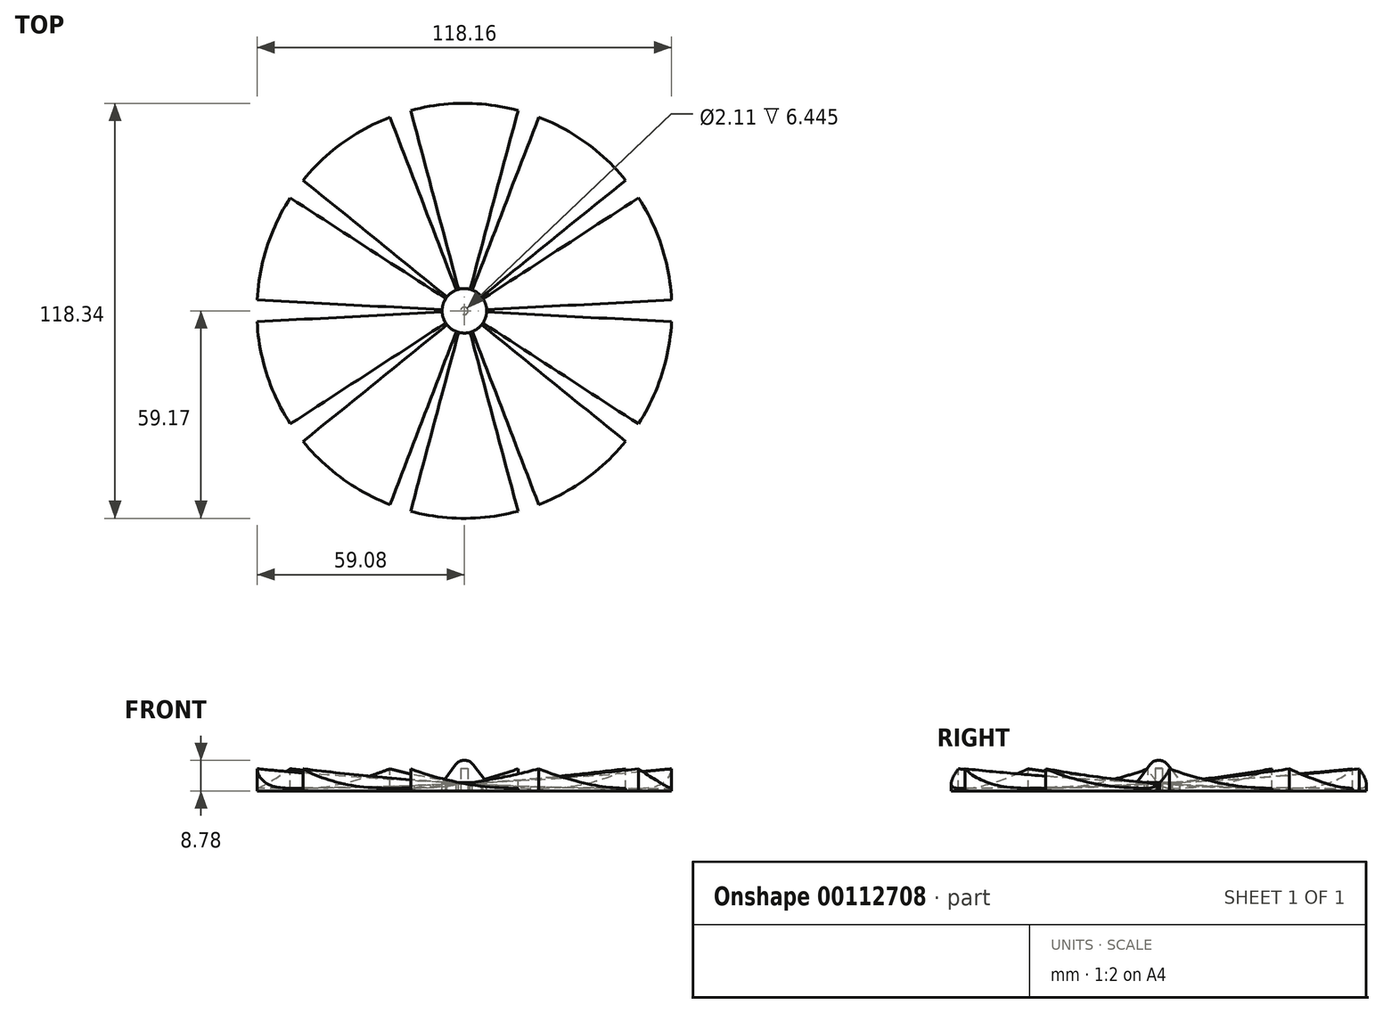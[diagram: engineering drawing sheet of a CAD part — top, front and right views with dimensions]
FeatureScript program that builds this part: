
annotation { "Feature Type Name" : "Feature", "Feature Type Description" : "" }
export const myFeature = defineFeature(function(context is Context, id is Id, definition is map)
    precondition{}
    {
        {
            var Q0;
            Q0=qCreatedBy(makeId("Top.planeOp"),FACE);
            var sketch = newSketch(context, id + "F0", { "sketchPlane" : qUnion([Q0])});
            skLineSegment(sketch, "E0", {"start": v(-15.31, -57.15) * mm, "end": v(15.31, -57.15) * mm, "construction": true});
            skLineSegment(sketch, "E1", {"start": v(0, 0) * mm, "end": v(0, -57.15) * mm, "construction": true});
            skArc(sketch, "E2", {"start": v(-15.31, -57.15) * mm, "mid": v(0, -59.17) * mm, "end": v(15.31, -57.15) * mm});
            skLineSegment(sketch, "E3", {"start": v(15.31, -57.15) * mm, "end": v(1.7, -6.35) * mm});
            skLineSegment(sketch, "E4", {"start": v(-15.31, -57.15) * mm, "end": v(-1.7, -6.35) * mm});
            skLineSegment(sketch, "E5", {"start": v(0, 0) * mm, "end": v(-1.7, -6.35) * mm});
            skLineSegment(sketch, "E6", {"start": v(0, 0) * mm, "end": v(1.7, -6.35) * mm});
            skLineSegment(sketch, "E7", {"start": v(1.7, -6.35) * mm, "end": v(-1.7, -6.35) * mm, "construction": true});
            skCircle(sketch, "E8", {"center": v(0, 0) * mm, "radius": 6.35 * mm, "construction": true});
            skSolve(sketch);
        }
        {
            var Q0;
            Q0 = qSketchRegion(id + "F0", true);
            extrude(context, id + "F1", {"entities" : qUnion([Q0]), "depth" : 6.35 * mm});
        }
        {
            var Q0;
            Q0=qCreatedBy(makeId("Front.planeOp"),FACE);
            var sketch = newSketch(context, id + "F2", { "sketchPlane" : qUnion([Q0])});
            skLineSegment(sketch, "E9.bottom", {"start": v(15.31, 0) * mm, "end": v(-15.31, 0) * mm, "construction": true});
            skLineSegment(sketch, "E9.top", {"start": v(15.31, 6.35) * mm, "end": v(-15.31, 6.35) * mm});
            skLineSegment(sketch, "E9.left", {"start": v(-15.31, 0) * mm, "end": v(-15.31, 6.35) * mm, "construction": true});
            skLineSegment(sketch, "E9.right", {"start": v(15.31, 0.8) * mm, "end": v(15.31, 6.35) * mm});
            skLineSegment(sketch, "E10", {"start": v(15.31, 0) * mm, "end": v(15.31, 0.8) * mm});
            skLineSegment(sketch, "E11", {"start": v(-15.31, 0.8) * mm, "end": v(15.31, 0.8) * mm, "construction": true});
            skArc(sketch, "E12", {"start": v(-15.31, 6.35) * mm, "mid": v(-0.25, 2.2) * mm, "end": v(15.31, 0.8) * mm});
            skSolve(sketch);
        }
        {
            var Q0;
            Q0 = qSketchRegion(id + "F2", true);
            var Q1;
            Q1=makeQuery(id+"F1.opExtrude","SWEPT_FACE",FACE,{"disambiguationData":[OSD([sQuery(id+"F0.wireOp",EDGE,"E2")])]});
            extrude(context, id + "F3", {"entities" : qUnion([Q0]), "operationType" : NewBodyOperationType.REMOVE, "endBound" : BoundingType.UP_TO_SURFACE, "endBoundEntityFace" : qUnion([Q1]), "depth" : 25.4 * mm});
        }
        {
            var Q0;
            Q0=makeQuery(id+"F1.opExtrude","CAP_FACE",FACE,{"disambiguationData":[OSD([sQuery(id+"F0.wireOp",EDGE,"E2"),sQuery(id+"F0.wireOp",EDGE,"E3"),sQuery(id+"F0.wireOp",EDGE,"E4"),sQuery(id+"F0.wireOp",EDGE,"E5"),sQuery(id+"F0.wireOp",EDGE,"E6")])],"isStart":true});
            var sketch = newSketch(context, id + "F4", { "sketchPlane" : qUnion([Q0])});
            skLineSegment(sketch, "E13", {"start": v(-15.31, 57.15) * mm, "end": v(-15.31, 57.15) * mm});
            skLineSegment(sketch, "E14", {"start": v(-15.31, 57.15) * mm, "end": v(0, 0) * mm});
            skLineSegment(sketch, "E15", {"start": v(0, 0) * mm, "end": v(15.31, 57.15) * mm});
            skLineSegment(sketch, "E16", {"start": v(15.31, 57.15) * mm, "end": v(15.31, 57.15) * mm});
            skArc(sketch, "E17", {"start": v(15.31, 57.15) * mm, "mid": v(0, 59.17) * mm, "end": v(-15.31, 57.15) * mm, "construction": true});
            skArc(sketch, "E18", {"start": v(-15.31, 57.15) * mm, "mid": v(0, -59.17) * mm, "end": v(15.31, 57.15) * mm});
            skSolve(sketch);
        }
        {
            var Q0;
            Q0 = qSketchRegion(id + "F4", true);
            extrude(context, id + "F5", {"entities" : qUnion([Q0]), "operationType" : NewBodyOperationType.ADD, "oppositeDirection" : true, "depth" : 6.35 * mm});
        }
        {
            var Q0;
            Q0=makeQuery(id+"F5.opExtrude","CAP_FACE",FACE,{"disambiguationData":[OSD([sQuery(id+"F4.wireOp",EDGE,"E13"),sQuery(id+"F4.wireOp",EDGE,"E14"),sQuery(id+"F4.wireOp",EDGE,"E15"),sQuery(id+"F4.wireOp",EDGE,"E16"),sQuery(id+"F4.wireOp",EDGE,"E18")])],"isStart":false});
            var sketch = newSketch(context, id + "F6", { "sketchPlane" : qUnion([Q0])});
            skCircle(sketch, "E19", {"center": v(0, 0) * mm, "radius": 6.35 * mm});
            skSolve(sketch);
        }
        {
            var Q0;
            Q0 = qSketchRegion(id + "F6", true);
            var Q1;
            Q1=makeQuery(id+"F5.boolean.opBoolean","MERGE",FACE,{"derivedFrom":[makeQuery(id+"F1.opExtrude","CAP_FACE",FACE,{"disambiguationData":[OSD([sQuery(id+"F0.wireOp",EDGE,"E2"),sQuery(id+"F0.wireOp",EDGE,"E3"),sQuery(id+"F0.wireOp",EDGE,"E4"),sQuery(id+"F0.wireOp",EDGE,"E5"),sQuery(id+"F0.wireOp",EDGE,"E6")])],"isStart":true}),makeQuery(id+"F5.opExtrude","CAP_FACE",FACE,{"disambiguationData":[OSD([sQuery(id+"F4.wireOp",EDGE,"E13"),sQuery(id+"F4.wireOp",EDGE,"E14"),sQuery(id+"F4.wireOp",EDGE,"E15"),sQuery(id+"F4.wireOp",EDGE,"E16"),sQuery(id+"F4.wireOp",EDGE,"E18")])],"isStart":true})]});
            extrude(context, id + "F7", {"entities" : qUnion([Q0]), "operationType" : NewBodyOperationType.ADD, "endBound" : BoundingType.UP_TO_SURFACE, "oppositeDirection" : true, "endBoundEntityFace" : qUnion([Q1]), "depth" : 25.4 * mm});
        }
        {
            var Q0;
            Q0=makeQuery(id+"F7.opExtrude","SWEPT_FACE",FACE,{"disambiguationData":[OSD([sQuery(id+"F6.wireOp",EDGE,"E19")])]});
            var Q1;
            Q1=makeQuery(id+"F3.boolean.opBoolean","COPY",FACE,{"derivedFrom":makeQuery(id+"F3.opExtrude","SWEPT_FACE",FACE,{"disambiguationData":[OSD([sQuery(id+"F2.wireOp",EDGE,"E12")])]})});
            var Q2;
            Q2=makeQuery(id+"F5.opExtrude","SWEPT_FACE",FACE,{"disambiguationData":[OSD([sQuery(id+"F4.wireOp",EDGE,"E15")])]});
            var Q3;
            Q3=makeQuery(id+"F5.opExtrude","SWEPT_FACE",FACE,{"disambiguationData":[OSD([sQuery(id+"F4.wireOp",EDGE,"E14")])]});
            var Q4;
            Q4=makeQuery(id+"F5.boolean.opBoolean","MERGE",FACE,{"derivedFrom":[makeQuery(id+"F1.opExtrude","SWEPT_FACE",FACE,{"disambiguationData":[OSD([sQuery(id+"F0.wireOp",EDGE,"E2")])]}),makeQuery(id+"F5.opExtrude","SWEPT_FACE",FACE,{"disambiguationData":[OSD([sQuery(id+"F4.wireOp",EDGE,"E18")])]})]});
            circularPattern(context, id + "F8", {"patternType" : PatternType.FACE, "faces" : qUnion([Q0, Q1, Q2, Q3]), "axis" : qUnion([Q4]), "angle" : 36 * degree, "instanceCount" : 10});
        }
        {
            var Q0;
            Q0=makeQuery(id+"F7.boolean.opBoolean","MERGE",FACE,{"derivedFrom":[makeQuery(id+"F5.opExtrude","CAP_FACE",FACE,{"disambiguationData":[OSD([sQuery(id+"F4.wireOp",EDGE,"E14"),sQuery(id+"F4.wireOp",EDGE,"E15"),sQuery(id+"F4.wireOp",EDGE,"E18")])],"isStart":false}),makeQuery(id+"F7.opExtrude","CAP_FACE",FACE,{"disambiguationData":[OSD([sQuery(id+"F6.wireOp",EDGE,"E19")])],"isStart":true})]});
            var sketch = newSketch(context, id + "F9", { "sketchPlane" : qUnion([Q0])});
            skCircle(sketch, "E20", {"center": v(0, 0) * mm, "radius": 6.35 * mm});
            skSolve(sketch);
        }
        {
            var Q0;
            {var subQ1=makeQuery(id+"F8.opPattern","COPY",EDGE,{"derivedFrom":makeQuery(id+"F5.opExtrude","CAP_EDGE",EDGE,{"disambiguationData":[OSD([sQuery(id+"F4.wireOp",EDGE,"E14")])],"isStart":false}),"instanceName":"2"});Q0=makeQuery(id+"F9.imprint","IMPRINT",FACE,{"disambiguationData":[TD([[makeQuery(id+"F9.imprint","IMPRINT",EDGE,{"derivedFrom":subQ1}),1.0]])]});}
            var Q1;
            {var subQ1=makeQuery(id+"F8.opPattern","COPY",EDGE,{"derivedFrom":makeQuery(id+"F5.opExtrude","CAP_EDGE",EDGE,{"disambiguationData":[OSD([sQuery(id+"F4.wireOp",EDGE,"E14")])],"isStart":false}),"instanceName":"1"});Q1=makeQuery(id+"F9.imprint","IMPRINT",FACE,{"disambiguationData":[TD([[makeQuery(id+"F9.imprint","IMPRINT",EDGE,{"derivedFrom":subQ1}),1.0]])]});}
            var Q2;
            {var subQ1=makeQuery(id+"F5.opExtrude","CAP_EDGE",EDGE,{"disambiguationData":[OSD([sQuery(id+"F4.wireOp",EDGE,"E14")])],"isStart":false});Q2=makeQuery(id+"F9.imprint","IMPRINT",FACE,{"disambiguationData":[TD([[makeQuery(id+"F9.imprint","IMPRINT",EDGE,{"derivedFrom":subQ1}),1.0]])]});}
            var Q3;
            {var subQ1=makeQuery(id+"F5.opExtrude","CAP_EDGE",EDGE,{"disambiguationData":[OSD([sQuery(id+"F4.wireOp",EDGE,"E15")])],"isStart":false});Q3=makeQuery(id+"F9.imprint","IMPRINT",FACE,{"disambiguationData":[TD([[makeQuery(id+"F9.imprint","IMPRINT",EDGE,{"derivedFrom":subQ1}),-1.0]])]});}
            var Q4;
            {var subQ1=makeQuery(id+"F8.opPattern","COPY",EDGE,{"derivedFrom":makeQuery(id+"F5.opExtrude","CAP_EDGE",EDGE,{"disambiguationData":[OSD([sQuery(id+"F4.wireOp",EDGE,"E14")])],"isStart":false}),"instanceName":"8"});Q4=makeQuery(id+"F9.imprint","IMPRINT",FACE,{"disambiguationData":[TD([[makeQuery(id+"F9.imprint","IMPRINT",EDGE,{"derivedFrom":subQ1}),1.0]])]});}
            var Q5;
            {var subQ1=makeQuery(id+"F8.opPattern","COPY",EDGE,{"derivedFrom":makeQuery(id+"F5.opExtrude","CAP_EDGE",EDGE,{"disambiguationData":[OSD([sQuery(id+"F4.wireOp",EDGE,"E14")])],"isStart":false}),"instanceName":"7"});Q5=makeQuery(id+"F9.imprint","IMPRINT",FACE,{"disambiguationData":[TD([[makeQuery(id+"F9.imprint","IMPRINT",EDGE,{"derivedFrom":subQ1}),1.0]])]});}
            var Q6;
            {var subQ1=makeQuery(id+"F8.opPattern","COPY",EDGE,{"derivedFrom":makeQuery(id+"F5.opExtrude","CAP_EDGE",EDGE,{"disambiguationData":[OSD([sQuery(id+"F4.wireOp",EDGE,"E14")])],"isStart":false}),"instanceName":"6"});Q6=makeQuery(id+"F9.imprint","IMPRINT",FACE,{"disambiguationData":[TD([[makeQuery(id+"F9.imprint","IMPRINT",EDGE,{"derivedFrom":subQ1}),1.0]])]});}
            var Q7;
            {var subQ1=makeQuery(id+"F8.opPattern","COPY",EDGE,{"derivedFrom":makeQuery(id+"F5.opExtrude","CAP_EDGE",EDGE,{"disambiguationData":[OSD([sQuery(id+"F4.wireOp",EDGE,"E14")])],"isStart":false}),"instanceName":"5"});Q7=makeQuery(id+"F9.imprint","IMPRINT",FACE,{"disambiguationData":[TD([[makeQuery(id+"F9.imprint","IMPRINT",EDGE,{"derivedFrom":subQ1}),1.0]])]});}
            var Q8;
            {var subQ1=makeQuery(id+"F8.opPattern","COPY",EDGE,{"derivedFrom":makeQuery(id+"F5.opExtrude","CAP_EDGE",EDGE,{"disambiguationData":[OSD([sQuery(id+"F4.wireOp",EDGE,"E14")])],"isStart":false}),"instanceName":"4"});Q8=makeQuery(id+"F9.imprint","IMPRINT",FACE,{"disambiguationData":[TD([[makeQuery(id+"F9.imprint","IMPRINT",EDGE,{"derivedFrom":subQ1}),1.0]])]});}
            var Q9;
            {var subQ1=makeQuery(id+"F8.opPattern","COPY",EDGE,{"derivedFrom":makeQuery(id+"F5.opExtrude","CAP_EDGE",EDGE,{"disambiguationData":[OSD([sQuery(id+"F4.wireOp",EDGE,"E14")])],"isStart":false}),"instanceName":"3"});Q9=makeQuery(id+"F9.imprint","IMPRINT",FACE,{"disambiguationData":[TD([[makeQuery(id+"F9.imprint","IMPRINT",EDGE,{"derivedFrom":subQ1}),1.0]])]});}
            var Q10;
            Q10=makeQuery(id+"F5.boolean.opBoolean","MERGE",FACE,{"derivedFrom":[makeQuery(id+"F1.opExtrude","CAP_FACE",FACE,{"disambiguationData":[OSD([sQuery(id+"F0.wireOp",EDGE,"E2"),sQuery(id+"F0.wireOp",EDGE,"E3"),sQuery(id+"F0.wireOp",EDGE,"E4"),sQuery(id+"F0.wireOp",EDGE,"E5"),sQuery(id+"F0.wireOp",EDGE,"E6")])],"isStart":true}),makeQuery(id+"F5.opExtrude","CAP_FACE",FACE,{"disambiguationData":[OSD([sQuery(id+"F4.wireOp",EDGE,"E14"),sQuery(id+"F4.wireOp",EDGE,"E15"),sQuery(id+"F4.wireOp",EDGE,"E18")])],"isStart":true})]});
            extrude(context, id + "F10", {"entities" : qUnion([Q0, Q1, Q2, Q3, Q4, Q5, Q6, Q7, Q8, Q9]), "operationType" : NewBodyOperationType.REMOVE, "endBound" : BoundingType.UP_TO_SURFACE, "oppositeDirection" : true, "endBoundEntityFace" : qUnion([Q10]), "depth" : 25.4 * mm});
        }
        {
            var Q0;
            Q0=makeQuery(id+"F7.boolean.opBoolean","MERGE",FACE,{"derivedFrom":[makeQuery(id+"F5.opExtrude","CAP_FACE",FACE,{"disambiguationData":[OSD([sQuery(id+"F4.wireOp",EDGE,"E14"),sQuery(id+"F4.wireOp",EDGE,"E15"),sQuery(id+"F4.wireOp",EDGE,"E18")])],"isStart":false}),makeQuery(id+"F7.opExtrude","CAP_FACE",FACE,{"disambiguationData":[OSD([sQuery(id+"F6.wireOp",EDGE,"E19")])],"isStart":true})]});
            extrude(context, id + "F11", {"entities" : qUnion([Q0]), "operationType" : NewBodyOperationType.ADD, "depth" : 2.43 * mm});
        }
        {
            var Q0;
            Q0=qCreatedBy(makeId("Front.planeOp"),FACE);
            var sketch = newSketch(context, id + "F12", { "sketchPlane" : qUnion([Q0])});
            skLineSegment(sketch, "E21.top", {"start": v(0, 15.13) * mm, "end": v(-6.35, 15.13) * mm});
            skLineSegment(sketch, "E21.left", {"start": v(0, 8.78) * mm, "end": v(0, 15.13) * mm});
            skLineSegment(sketch, "E21.right", {"start": v(-6.35, 2.43) * mm, "end": v(-6.35, 15.13) * mm});
            skLineSegment(sketch, "E22", {"start": v(0, 8.78) * mm, "end": v(0, 2.43) * mm, "construction": true});
            skLineSegment(sketch, "E23", {"start": v(0, 2.43) * mm, "end": v(-6.35, 2.43) * mm, "construction": true});
            skArc(sketch, "E24", {"start": v(0, 8.78) * mm, "mid": v(-1.42, 8.45) * mm, "end": v(-2.54, 7.51) * mm});
            skLineSegment(sketch, "E25", {"start": v(-2.54, 7.51) * mm, "end": v(-6.35, 2.43) * mm});
            skSolve(sketch);
        }
        {
            var Q0;
            Q0 = qSketchRegion(id + "F12", true);
            var Q1;
            Q1=makeQuery(id+"F11.opExtrude","CAP_EDGE",EDGE,{"disambiguationData":[OSD([sQuery(id+"F6.wireOp",EDGE,"E19"),sQuery(id+"F9.wireOp",EDGE,"E20")])],"isStart":false});
            revolve(context, id + "F13", {"operationType" : NewBodyOperationType.REMOVE, "entities" : qUnion([Q0]), "axis" : qUnion([Q1]), "revolveType" : RevolveType.FULL, "oppositeDirection" : true});
        }
        {
            var Q0;
            Q0=makeQuery(id+"F5.boolean.opBoolean","MERGE",FACE,{"derivedFrom":[makeQuery(id+"F1.opExtrude","CAP_FACE",FACE,{"disambiguationData":[OSD([sQuery(id+"F0.wireOp",EDGE,"E2"),sQuery(id+"F0.wireOp",EDGE,"E3"),sQuery(id+"F0.wireOp",EDGE,"E4"),sQuery(id+"F0.wireOp",EDGE,"E5"),sQuery(id+"F0.wireOp",EDGE,"E6")])],"isStart":true}),makeQuery(id+"F5.opExtrude","CAP_FACE",FACE,{"disambiguationData":[OSD([sQuery(id+"F4.wireOp",EDGE,"E14"),sQuery(id+"F4.wireOp",EDGE,"E15"),sQuery(id+"F4.wireOp",EDGE,"E18")])],"isStart":true})]});
            var sketch = newSketch(context, id + "F14", { "sketchPlane" : qUnion([Q0])});
            skCircle(sketch, "E26", {"center": v(0, 0) * mm, "radius": 1.05 * mm});
            skSolve(sketch);
        }
        {
            var Q0;
            Q0 = qSketchRegion(id + "F14", true);
            extrude(context, id + "F15", {"entities" : qUnion([Q0]), "operationType" : NewBodyOperationType.REMOVE, "oppositeDirection" : true, "depth" : 6.45 * mm});
        }
    });
